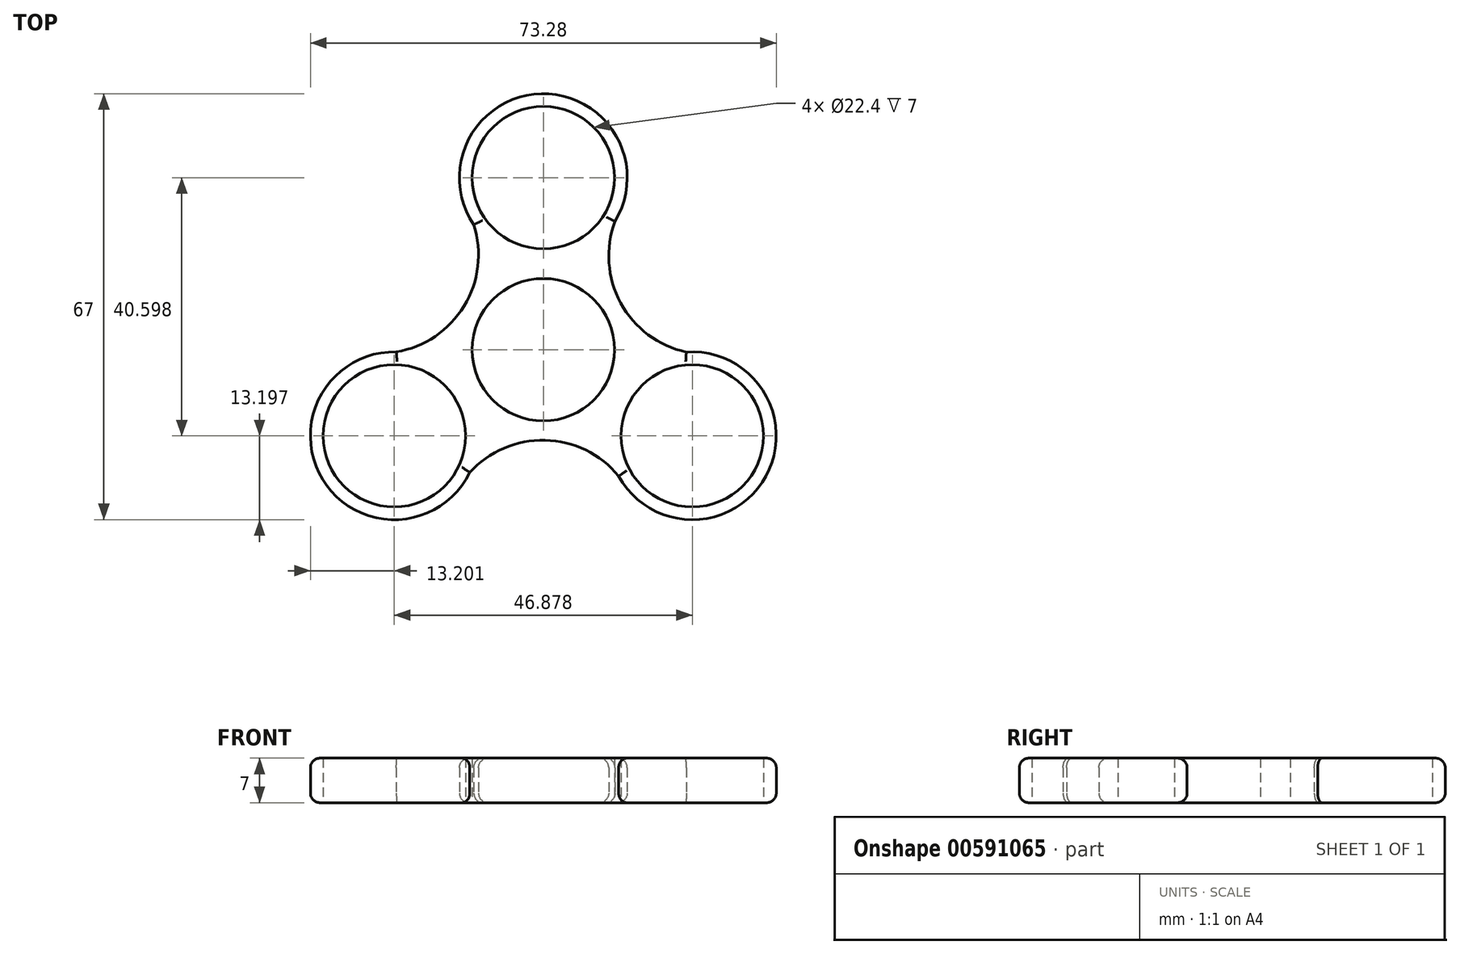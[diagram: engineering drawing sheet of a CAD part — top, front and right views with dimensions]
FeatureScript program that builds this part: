
annotation { "Feature Type Name" : "Feature", "Feature Type Description" : "" }
export const myFeature = defineFeature(function(context is Context, id is Id, definition is map)
    precondition{}
    {
        {
            var Q0;
            Q0=qCreatedBy(makeId("Top.planeOp"),FACE);
            var sketch = newSketch(context, id + "F0", { "sketchPlane" : qUnion([Q0])});
            skCircle(sketch, "E0", {"center": v(0, 0) * mm, "radius": 11.2 * mm});
            skCircle(sketch, "E1", {"center": v(0, 27.07) * mm, "radius": 11.2 * mm});
            skArc(sketch, "E2", {"start": v(11.27, 20.2) * mm, "mid": v(-0.31, 40.26) * mm, "end": v(-10.93, 19.67) * mm});
            skArc(sketch, "E3.1.0", {"start": v(-23.12, -0.34) * mm, "mid": v(-34.71, -20.4) * mm, "end": v(-11.57, -19.3) * mm});
            skCircle(sketch, "E3.1.1", {"center": v(-23.44, -13.53) * mm, "radius": 11.2 * mm});
            skArc(sketch, "E3.2.0", {"start": v(11.85, -19.85) * mm, "mid": v(35.02, -19.86) * mm, "end": v(22.5, -0.37) * mm});
            skCircle(sketch, "E3.2.1", {"center": v(23.44, -13.53) * mm, "radius": 11.2 * mm});
            skArc(sketch, "E4", {"start": v(11.27, 20.2) * mm, "mid": v(12.19, 7.35) * mm, "end": v(22.5, -0.37) * mm});
            skArc(sketch, "E5.1.0", {"start": v(-23.12, -0.34) * mm, "mid": v(-12.46, 6.88) * mm, "end": v(-10.93, 19.67) * mm});
            skArc(sketch, "E5.2.0", {"start": v(11.85, -19.85) * mm, "mid": v(0.27, -14.23) * mm, "end": v(-11.57, -19.3) * mm});
            skSolve(sketch);
        }
        {
            var Q0;
            Q0=makeQuery(id+"F0.imprint","IMPRINT",FACE,{"disambiguationData":[TD([[makeQuery(id+"F0.imprint","IMPRINT",EDGE,{"derivedFrom":sQuery(id+"F0.wireOp",EDGE,"E0")}),-1.0]])]});
            extrude(context, id + "F1", {"entities" : qUnion([Q0]), "depth" : 7 * mm, "offsetDistance" : 25 * mm});
        }
        {
            var Q0;
            Q0=makeQuery(id+"F1.opExtrude","CAP_EDGE",EDGE,{"disambiguationData":[OSD([sQuery(id+"F0.wireOp",EDGE,"E5.2.0")])],"isStart":false});
            var Q1;
            Q1=makeQuery(id+"F1.opExtrude","CAP_EDGE",EDGE,{"disambiguationData":[OSD([sQuery(id+"F0.wireOp",EDGE,"E5.2.0")])],"isStart":true});
            var Q2;
            Q2=makeQuery(id+"F1.opExtrude","CAP_EDGE",EDGE,{"disambiguationData":[OSD([sQuery(id+"F0.wireOp",EDGE,"E3.1.0")])],"isStart":false});
            var Q3;
            Q3=makeQuery(id+"F1.opExtrude","CAP_EDGE",EDGE,{"disambiguationData":[OSD([sQuery(id+"F0.wireOp",EDGE,"E5.1.0")])],"isStart":false});
            var Q4;
            Q4=makeQuery(id+"F1.opExtrude","CAP_EDGE",EDGE,{"disambiguationData":[OSD([sQuery(id+"F0.wireOp",EDGE,"E2")])],"isStart":false});
            var Q5;
            Q5=makeQuery(id+"F1.opExtrude","CAP_EDGE",EDGE,{"disambiguationData":[OSD([sQuery(id+"F0.wireOp",EDGE,"E3.2.0")])],"isStart":false});
            var Q6;
            Q6=makeQuery(id+"F1.opExtrude","CAP_EDGE",EDGE,{"disambiguationData":[OSD([sQuery(id+"F0.wireOp",EDGE,"E4")])],"isStart":false});
            fillet(context, id + "F2", {"entities" : qUnion([Q0, Q1, Q2, Q3, Q4, Q5, Q6]), "radius" : 1.5 * mm, "tangentPropagation" : true, "allowEdgeOverflow" : false});
        }
        {
            var Q0;
            Q0=makeQuery(id+"F1.opExtrude","CAP_EDGE",EDGE,{"disambiguationData":[OSD([sQuery(id+"F0.wireOp",EDGE,"E3.1.0")])],"isStart":true});
            var Q1;
            {var subQ0=sQuery(id+"F0.wireOp",EDGE,"E5.2.0");Q1=makeQuery(id+"F2.opFillet","BLEND_EDGE",EDGE,{"blendedFrom":[makeQuery(id+"F1.opExtrude","CAP_EDGE",EDGE,{"disambiguationData":[OSD([subQ0])],"isStart":true}),makeQuery(id+"F1.opExtrude","CAP_FACE",FACE,{"disambiguationData":[OSD([sQuery(id+"F0.wireOp",EDGE,"E0"),sQuery(id+"F0.wireOp",EDGE,"E1"),sQuery(id+"F0.wireOp",EDGE,"E2"),sQuery(id+"F0.wireOp",EDGE,"E3.1.0"),sQuery(id+"F0.wireOp",EDGE,"E3.1.1"),sQuery(id+"F0.wireOp",EDGE,"E3.2.0"),sQuery(id+"F0.wireOp",EDGE,"E3.2.1"),sQuery(id+"F0.wireOp",EDGE,"E4"),sQuery(id+"F0.wireOp",EDGE,"E5.1.0"),subQ0])],"isStart":true})],"blendedInto":[makeQuery(id+"F1.opExtrude","CAP_FACE",FACE,{"disambiguationData":[OSD([sQuery(id+"F0.wireOp",EDGE,"E0"),sQuery(id+"F0.wireOp",EDGE,"E1"),sQuery(id+"F0.wireOp",EDGE,"E2"),sQuery(id+"F0.wireOp",EDGE,"E3.1.0"),sQuery(id+"F0.wireOp",EDGE,"E3.1.1"),sQuery(id+"F0.wireOp",EDGE,"E3.2.0"),sQuery(id+"F0.wireOp",EDGE,"E3.2.1"),sQuery(id+"F0.wireOp",EDGE,"E4"),sQuery(id+"F0.wireOp",EDGE,"E5.1.0"),subQ0])],"isStart":true})]});}
            var Q2;
            Q2=makeQuery(id+"F1.opExtrude","CAP_EDGE",EDGE,{"disambiguationData":[OSD([sQuery(id+"F0.wireOp",EDGE,"E3.2.0")])],"isStart":true});
            var Q3;
            Q3=makeQuery(id+"F1.opExtrude","CAP_EDGE",EDGE,{"disambiguationData":[OSD([sQuery(id+"F0.wireOp",EDGE,"E4")])],"isStart":true});
            var Q4;
            Q4=makeQuery(id+"F1.opExtrude","CAP_EDGE",EDGE,{"disambiguationData":[OSD([sQuery(id+"F0.wireOp",EDGE,"E2")])],"isStart":true});
            var Q5;
            Q5=makeQuery(id+"F1.opExtrude","CAP_EDGE",EDGE,{"disambiguationData":[OSD([sQuery(id+"F0.wireOp",EDGE,"E5.1.0")])],"isStart":true});
            fillet(context, id + "F3", {"entities" : qUnion([Q0, Q1, Q2, Q3, Q4, Q5]), "radius" : 1.5 * mm, "tangentPropagation" : true, "allowEdgeOverflow" : false});
        }
    });
